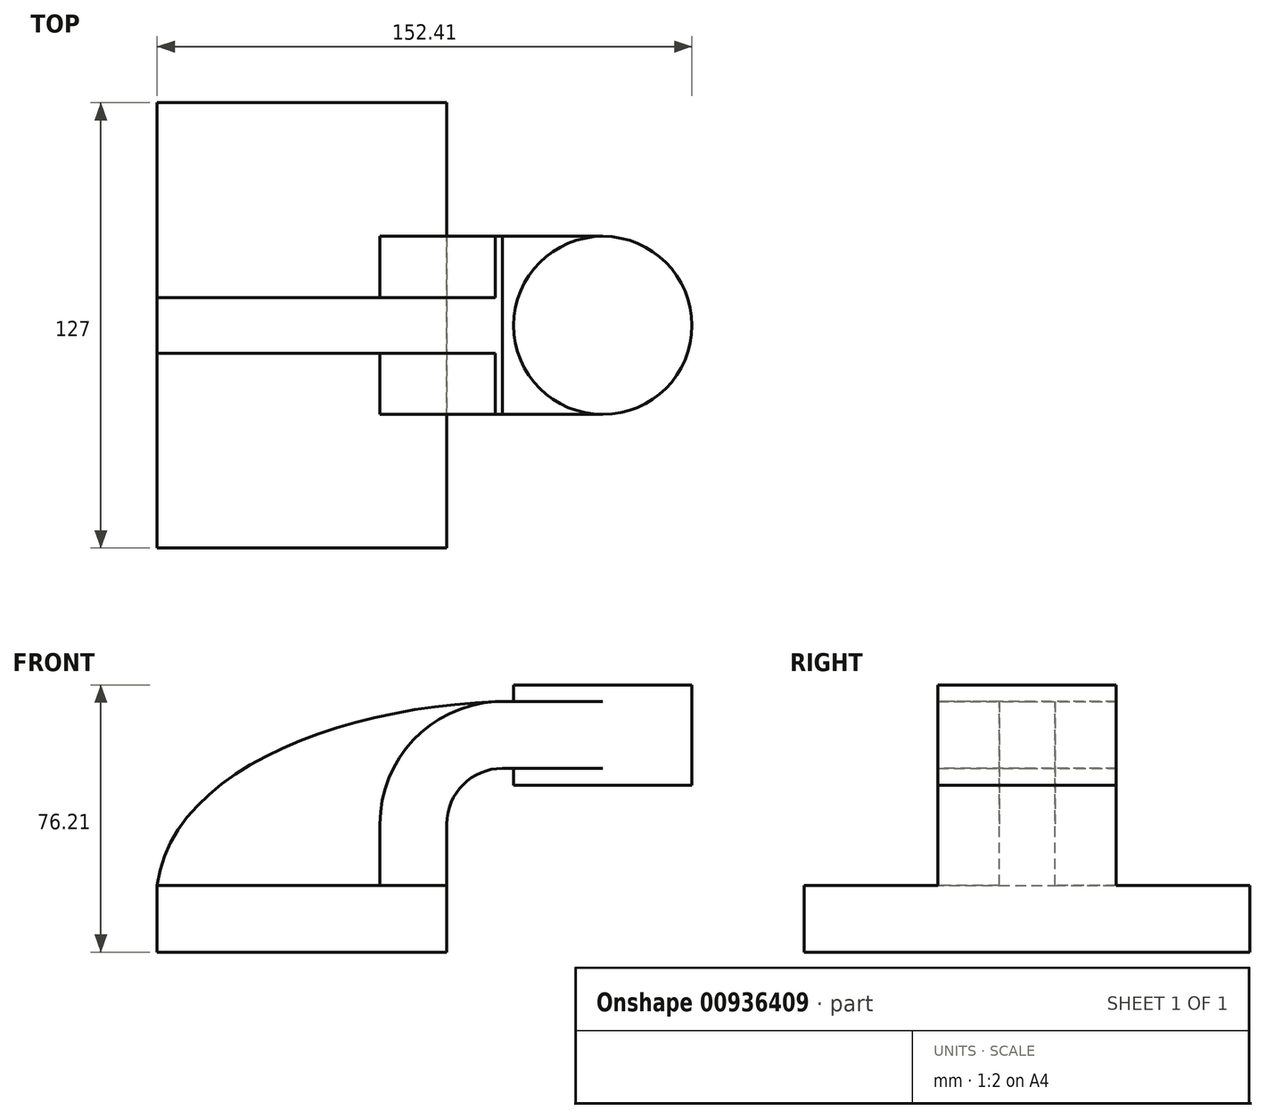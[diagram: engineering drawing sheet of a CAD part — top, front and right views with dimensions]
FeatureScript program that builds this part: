
annotation { "Feature Type Name" : "Feature", "Feature Type Description" : "" }
export const myFeature = defineFeature(function(context is Context, id is Id, definition is map)
    precondition{}
    {
        {
            var Q0;
            Q0=qCreatedBy(makeId("Front.planeOp"),FACE);
            var sketch = newSketch(context, id + "F0", { "sketchPlane" : qUnion([Q0])});
            skLineSegment(sketch, "E0.bottom", {"start": v(-41.28, -9.53) * mm, "end": v(41.28, -9.53) * mm});
            skLineSegment(sketch, "E0.top", {"start": v(-41.28, 9.53) * mm, "end": v(41.28, 9.53) * mm});
            skLineSegment(sketch, "E0.left", {"start": v(-41.28, -9.53) * mm, "end": v(-41.28, 9.53) * mm});
            skLineSegment(sketch, "E0.right", {"start": v(41.28, -9.53) * mm, "end": v(41.28, 9.52) * mm});
            skPoint(sketch, "E0.middle", {"position": v(0, 0) * mm});
            skLineSegment(sketch, "E1.bottom", {"start": v(111.12, 66.67) * mm, "end": v(60.32, 66.67) * mm});
            skLineSegment(sketch, "E1.top", {"start": v(111.12, 38.1) * mm, "end": v(60.32, 38.1) * mm});
            skLineSegment(sketch, "E1.left", {"start": v(111.12, 66.68) * mm, "end": v(111.12, 38.1) * mm});
            skLineSegment(sketch, "E1.right", {"start": v(60.32, 66.67) * mm, "end": v(60.32, 38.1) * mm});
            skPoint(sketch, "E1.middle", {"position": v(85.72, 52.39) * mm});
            skLineSegment(sketch, "E2", {"start": v(41.28, 9.53) * mm, "end": v(41.28, 27) * mm});
            skArc(sketch, "E3", {"start": v(41.28, 27) * mm, "mid": v(45.92, 38.23) * mm, "end": v(57.15, 42.88) * mm});
            skLineSegment(sketch, "E4", {"start": v(57.15, 42.88) * mm, "end": v(85.72, 42.88) * mm});
            skLineSegment(sketch, "E5.0", {"start": v(57.15, 61.93) * mm, "end": v(85.72, 61.93) * mm});
            skArc(sketch, "E5.1", {"start": v(22.23, 27) * mm, "mid": v(32.45, 51.7) * mm, "end": v(57.15, 61.93) * mm});
            skLineSegment(sketch, "E5.2", {"start": v(22.23, 9.53) * mm, "end": v(22.23, 27) * mm});
            skLineSegment(sketch, "E6", {"start": v(85.72, 38.1) * mm, "end": v(85.72, 66.67) * mm});
            skFitSpline(sketch, "E7", {"points": [v(-41.28, 9.53) * mm, v(57.15, 61.93) * mm], "startDerivative": vector(13.04, 100.66) * mm, "endDerivative": vector(132.72, 3.2) * mm});
            skSolve(sketch);
        }
        {
            var Q0;
            Q0=makeQuery(id+"F0.imprint","IMPRINT",FACE,{"disambiguationData":[TD([[makeQuery(id+"F0.imprint","IMPRINT",EDGE,{"derivedFrom":sQuery(id+"F0.wireOp",EDGE,"E0.bottom")}),1.0]])]});
            extrude(context, id + "F1", {"entities" : qUnion([Q0]), "depth" : 127 * mm, "offsetDistance" : 25.4 * mm, "symmetric" : true});
        }
        {
            var Q0;
            {var subQ0=sQuery(id+"F0.wireOp",EDGE,"E5.0");var subQ1=sQuery(id+"F0.wireOp",EDGE,"E1.right");var subQ2=makeQuery(id+"F0.imprint","INTERSECT",VERTEX,{"derivedFrom":[subQ1,subQ0]});Q0=makeQuery(id+"F0.imprint","IMPRINT",FACE,{"disambiguationData":[TD([[makeQuery(id+"F0.imprint","IMPRINT",EDGE,{"disambiguationData":[TD([[subQ2,-1.0]])],"derivedFrom":subQ1}),1.0]])]});}
            var sketch = newSketch(context, id + "F2", { "sketchPlane" : qUnion([Q0])});
            skSolve(sketch);
        }
        {
            var Q0;
            {var subQ0=sQuery(id+"F0.wireOp",EDGE,"E5.0");var subQ1=sQuery(id+"F0.wireOp",EDGE,"E1.right");var subQ2=makeQuery(id+"F0.imprint","INTERSECT",VERTEX,{"derivedFrom":[subQ1,subQ0]});Q0=makeQuery(id+"F2.imprint","IMPRINT",FACE,{"disambiguationData":[TD([[makeQuery(id+"F2.imprint","IMPRINT",EDGE,{"derivedFrom":makeQuery(id+"F0.imprint","IMPRINT",EDGE,{"disambiguationData":[TD([[subQ2,-1.0]])],"derivedFrom":subQ1})}),1.0]])]});}
            var Q1;
            {var subQ1=sQuery(id+"F0.wireOp",EDGE,"E2");Q1=makeQuery(id+"F0.imprint","IMPRINT",FACE,{"disambiguationData":[TD([[makeQuery(id+"F0.imprint","IMPRINT",EDGE,{"derivedFrom":subQ1}),1.0]])]});}
            extrude(context, id + "F3", {"entities" : qUnion([Q0, Q1]), "operationType" : NewBodyOperationType.ADD, "oppositeDirection" : true, "depth" : 50.8 * mm, "offsetDistance" : 25.4 * mm, "symmetric" : true});
        }
        {
            var Q0;
            {var subQ3=sQuery(id+"F0.wireOp",EDGE,"E5.2");Q0=makeQuery(id+"F0.imprint","IMPRINT",FACE,{"disambiguationData":[TD([[makeQuery(id+"F0.imprint","IMPRINT",EDGE,{"derivedFrom":subQ3}),1.0]])]});}
            var sketch = newSketch(context, id + "F4", { "sketchPlane" : qUnion([Q0])});
            skSolve(sketch);
        }
        {
            var Q0;
            Q0 = qSketchRegion(id + "F4", true);
            var Q1;
            {var subQ3=sQuery(id+"F0.wireOp",EDGE,"E5.2");Q1=makeQuery(id+"F0.imprint","IMPRINT",FACE,{"disambiguationData":[TD([[makeQuery(id+"F0.imprint","IMPRINT",EDGE,{"derivedFrom":subQ3}),1.0]])]});}
            extrude(context, id + "F5", {"entities" : qUnion([Q0, Q1]), "operationType" : NewBodyOperationType.ADD, "depth" : 15.88 * mm, "offsetDistance" : 25.4 * mm, "symmetric" : true});
        }
        {
            var Q0;
            {var subQ0=sQuery(id+"F0.wireOp",EDGE,"E1.left");Q0=makeQuery(id+"F0.imprint","IMPRINT",FACE,{"disambiguationData":[TD([[makeQuery(id+"F0.imprint","IMPRINT",EDGE,{"derivedFrom":subQ0}),-1.0]])]});}
            var sketch = newSketch(context, id + "F6", { "sketchPlane" : qUnion([Q0])});
            skSolve(sketch);
        }
        {
            var Q0;
            {var subQ4=sQuery(id+"F0.wireOp",EDGE,"E1.left");Q0=makeQuery(id+"F6.imprint","IMPRINT",FACE,{"disambiguationData":[TD([[makeQuery(id+"F6.imprint","IMPRINT",EDGE,{"derivedFrom":makeQuery(id+"F0.imprint","IMPRINT",EDGE,{"derivedFrom":subQ4})}),-1.0]])]});}
            var Q1;
            Q1=sQuery(id+"F0.wireOp",EDGE,"E6");
            revolve(context, id + "F7", {"operationType" : NewBodyOperationType.ADD, "surfaceOperationType" : NewSurfaceOperationType.NEW, "entities" : qUnion([Q0]), "axis" : qUnion([Q1]), "revolveType" : RevolveType.FULL});
        }
    });
